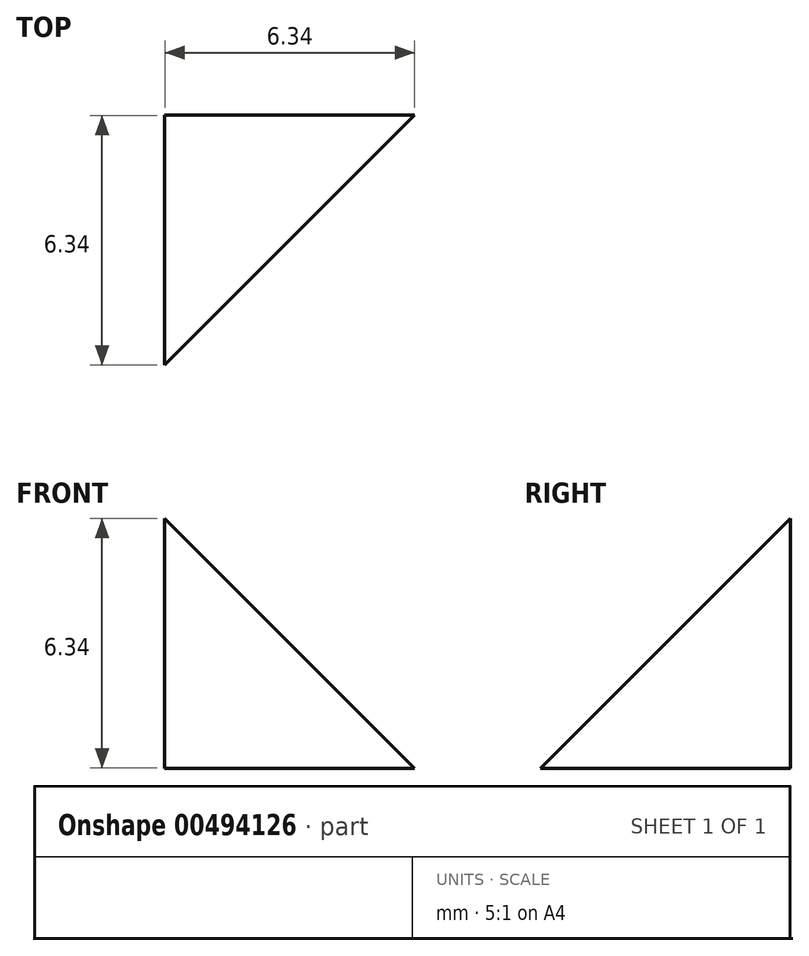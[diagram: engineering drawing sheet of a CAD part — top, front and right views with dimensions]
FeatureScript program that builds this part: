
annotation { "Feature Type Name" : "Feature", "Feature Type Description" : "" }
export const myFeature = defineFeature(function(context is Context, id is Id, definition is map)
    precondition{}
    {
        {
            var Q0;
            Q0=qCreatedBy(makeId("Right.planeOp"),FACE);
            var sketch = newSketch(context, id + "F0", { "sketchPlane" : qUnion([Q0])});
            skLineSegment(sketch, "E0.bottom", {"start": v(-3.17, 3.17) * mm, "end": v(3.18, 3.17) * mm});
            skLineSegment(sketch, "E0.top", {"start": v(-3.17, -3.18) * mm, "end": v(3.18, -3.18) * mm});
            skLineSegment(sketch, "E0.left", {"start": v(-3.17, 3.18) * mm, "end": v(-3.17, -3.18) * mm});
            skLineSegment(sketch, "E0.right", {"start": v(3.18, 3.17) * mm, "end": v(3.18, -3.18) * mm});
            skPoint(sketch, "E0.middle", {"position": v(0, 0) * mm});
            skSolve(sketch);
        }
        {
            var Q0;
            Q0=makeQuery(id+"F0.imprint","IMPRINT",FACE,{"disambiguationData":[TD([[makeQuery(id+"F0.imprint","IMPRINT",EDGE,{"derivedFrom":sQuery(id+"F0.wireOp",EDGE,"E0.bottom")}),-1.0]])]});
            extrude(context, id + "F1", {"entities" : qUnion([Q0]), "endBound" : BoundingType.SYMMETRIC, "depth" : 6.35 * mm});
        }
        {
            var Q0;
            Q0=makeQuery(id+"F1.opExtrude","SWEPT_EDGE",EDGE,{"disambiguationData":[OSD([sQuery(id+"F0.wireOp",EDGE,"E0.bottom"),sQuery(id+"F0.wireOp",EDGE,"E0.left")])]});
            var Q1;
            Q1=makeQuery(id+"F1.opExtrude","CAP_EDGE",EDGE,{"disambiguationData":[OSD([sQuery(id+"F0.wireOp",EDGE,"E0.bottom")])],"isStart":false});
            var Q2;
            Q2=makeQuery(id+"F1.opExtrude","CAP_EDGE",EDGE,{"disambiguationData":[OSD([sQuery(id+"F0.wireOp",EDGE,"E0.left")])],"isStart":false});
            chamfer(context, id + "F2", {"entities" : qUnion([Q0, Q1, Q2]), "width" : 6.35 * mm, "tangentPropagation" : true});
        }
    });
